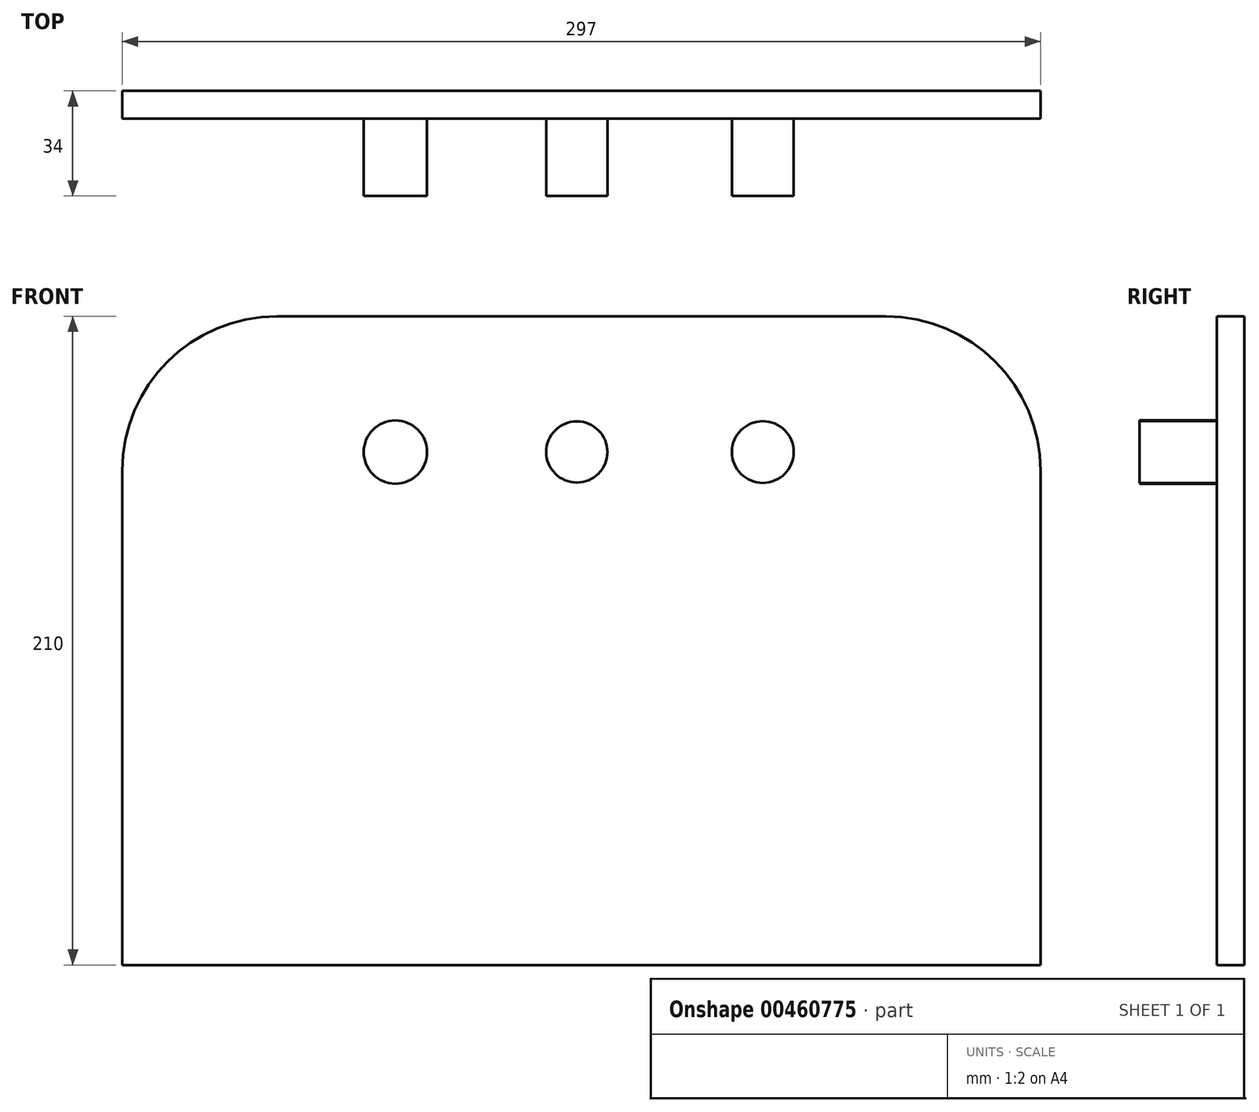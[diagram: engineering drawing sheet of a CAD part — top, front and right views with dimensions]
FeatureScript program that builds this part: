
annotation { "Feature Type Name" : "Feature", "Feature Type Description" : "" }
export const myFeature = defineFeature(function(context is Context, id is Id, definition is map)
    precondition{}
    {
        {
            var Q0;
            Q0=qCreatedBy(makeId("Front.planeOp"),FACE);
            var sketch = newSketch(context, id + "F0", { "sketchPlane" : qUnion([Q0])});
            skLineSegment(sketch, "E0.bottom", {"start": v(-137.17, 143.36) * mm, "end": v(59.83, 143.36) * mm});
            skLineSegment(sketch, "E0.top", {"start": v(-187.17, -66.64) * mm, "end": v(109.83, -66.64) * mm});
            skLineSegment(sketch, "E0.left", {"start": v(-187.17, 93.36) * mm, "end": v(-187.17, -66.64) * mm});
            skLineSegment(sketch, "E0.right", {"start": v(109.83, 93.36) * mm, "end": v(109.83, -66.64) * mm});
            skPoint(sketch, "E1.visualSharp", {"position": v(-187.17, 143.36) * mm});
            skArc(sketch, "E1.filletArc", {"start": v(-137.17, 143.36) * mm, "mid": v(-172.53, 128.72) * mm, "end": v(-187.17, 93.36) * mm});
            skPoint(sketch, "E2.visualSharp", {"position": v(109.83, 143.36) * mm});
            skArc(sketch, "E2.filletArc", {"start": v(109.83, 93.36) * mm, "mid": v(95.18, 128.72) * mm, "end": v(59.83, 143.36) * mm});
            skSolve(sketch);
        }
        {
            var Q0;
            Q0=makeQuery(id+"F0.imprint","IMPRINT",FACE,{"disambiguationData":[TD([[makeQuery(id+"F0.imprint","IMPRINT",EDGE,{"derivedFrom":sQuery(id+"F0.wireOp",EDGE,"E0.bottom")}),-1.0]])]});
            extrude(context, id + "F1", {"entities" : qUnion([Q0]), "depth" : 9 * mm});
        }
        {
            var Q0;
            Q0=makeQuery(id+"F1.opExtrude","CAP_FACE",FACE,{"disambiguationData":[OSD([sQuery(id+"F0.wireOp",EDGE,"E0.bottom"),sQuery(id+"F0.wireOp",EDGE,"E0.top"),sQuery(id+"F0.wireOp",EDGE,"E0.left"),sQuery(id+"F0.wireOp",EDGE,"E0.right"),sQuery(id+"F0.wireOp",EDGE,"E1.filletArc"),sQuery(id+"F0.wireOp",EDGE,"E2.filletArc")])],"isStart":false});
            var sketch = newSketch(context, id + "F2", { "sketchPlane" : qUnion([Q0])});
            skCircle(sketch, "E3", {"center": v(-98.85, 99.44) * mm, "radius": 10.25 * mm});
            skCircle(sketch, "E4", {"center": v(-40.15, 99.44) * mm, "radius": 9.9 * mm});
            skCircle(sketch, "E5", {"center": v(20.02, 99.44) * mm, "radius": 10 * mm});
            skSolve(sketch);
        }
        {
            var Q0;
            Q0=makeQuery(id+"F2.imprint","IMPRINT",FACE,{"disambiguationData":[TD([[makeQuery(id+"F2.imprint","IMPRINT",EDGE,{"derivedFrom":sQuery(id+"F2.wireOp",EDGE,"E3")}),1.0]])]});
            var Q1;
            Q1=makeQuery(id+"F2.imprint","IMPRINT",FACE,{"disambiguationData":[TD([[makeQuery(id+"F2.imprint","IMPRINT",EDGE,{"derivedFrom":sQuery(id+"F2.wireOp",EDGE,"E4")}),1.0]])]});
            var Q2;
            Q2=makeQuery(id+"F2.imprint","IMPRINT",FACE,{"disambiguationData":[TD([[makeQuery(id+"F2.imprint","IMPRINT",EDGE,{"derivedFrom":sQuery(id+"F2.wireOp",EDGE,"E5")}),1.0]])]});
            extrude(context, id + "F3", {"entities" : qUnion([Q0, Q1, Q2]), "operationType" : NewBodyOperationType.ADD, "depth" : 25 * mm});
        }
    });
